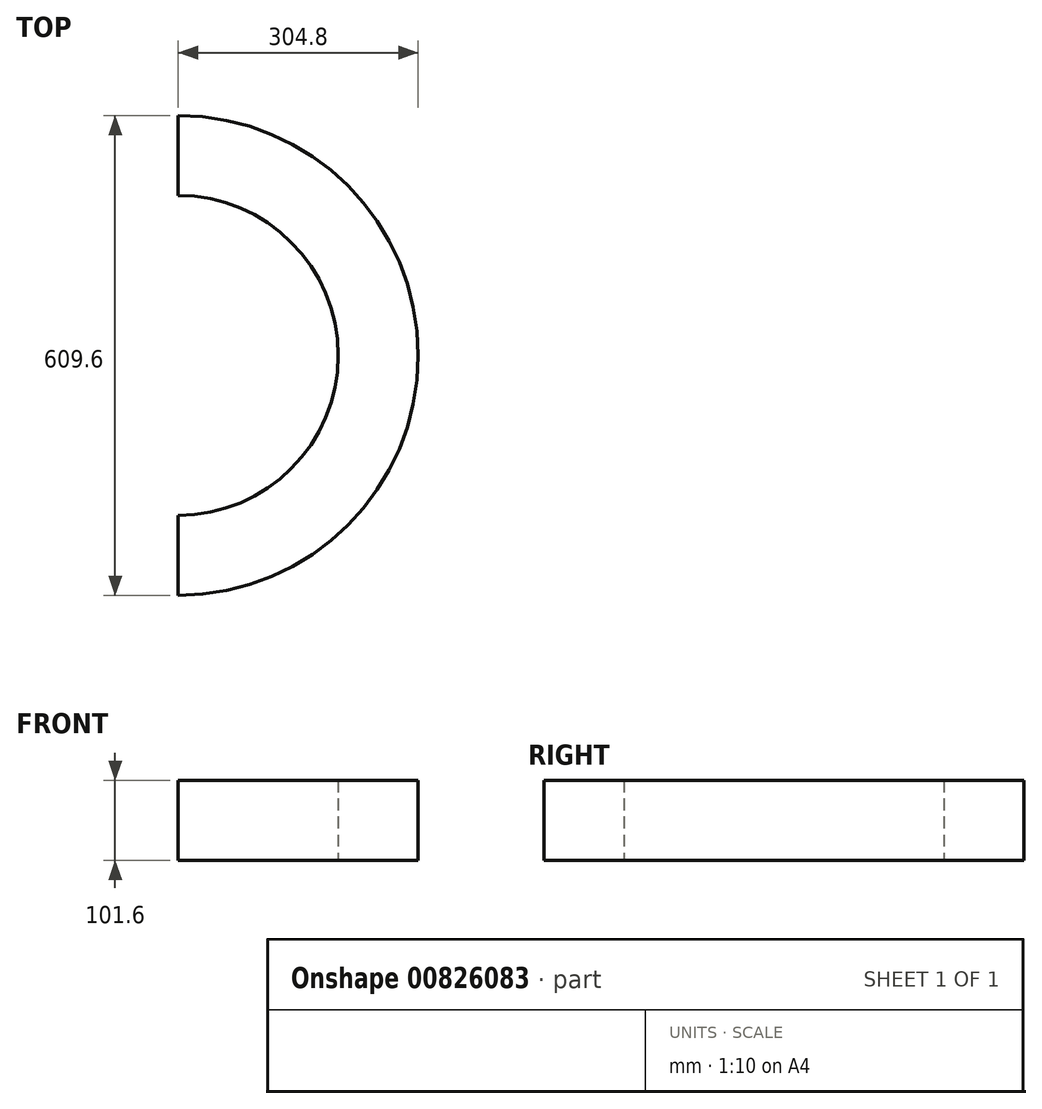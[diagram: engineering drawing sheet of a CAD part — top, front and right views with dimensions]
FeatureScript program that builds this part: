
annotation { "Feature Type Name" : "Feature", "Feature Type Description" : "" }
export const myFeature = defineFeature(function(context is Context, id is Id, definition is map)
    precondition{}
    {
        {
            var Q0;
            Q0=qCreatedBy(makeId("Top.planeOp"),FACE);
            var sketch = newSketch(context, id + "F0", { "sketchPlane" : qUnion([Q0])});
            skArc(sketch, "E0", {"start": v(0, 0) * mm, "mid": v(304.8, 304.8) * mm, "end": v(0, 609.6) * mm});
            skLineSegment(sketch, "E1", {"start": v(0, 0) * mm, "end": v(0, 101.6) * mm});
            skLineSegment(sketch, "E2", {"start": v(0, 609.6) * mm, "end": v(0, 508) * mm});
            skArc(sketch, "E3", {"start": v(0, 101.6) * mm, "mid": v(203.2, 304.8) * mm, "end": v(0, 508) * mm});
            skSolve(sketch);
        }
        {
            var Q0;
            Q0 = qSketchRegion(id + "F0", true);
            extrude(context, id + "F1", {"entities" : qUnion([Q0]), "depth" : 101.6 * mm, "offsetDistance" : 25 * mm});
        }
    });
